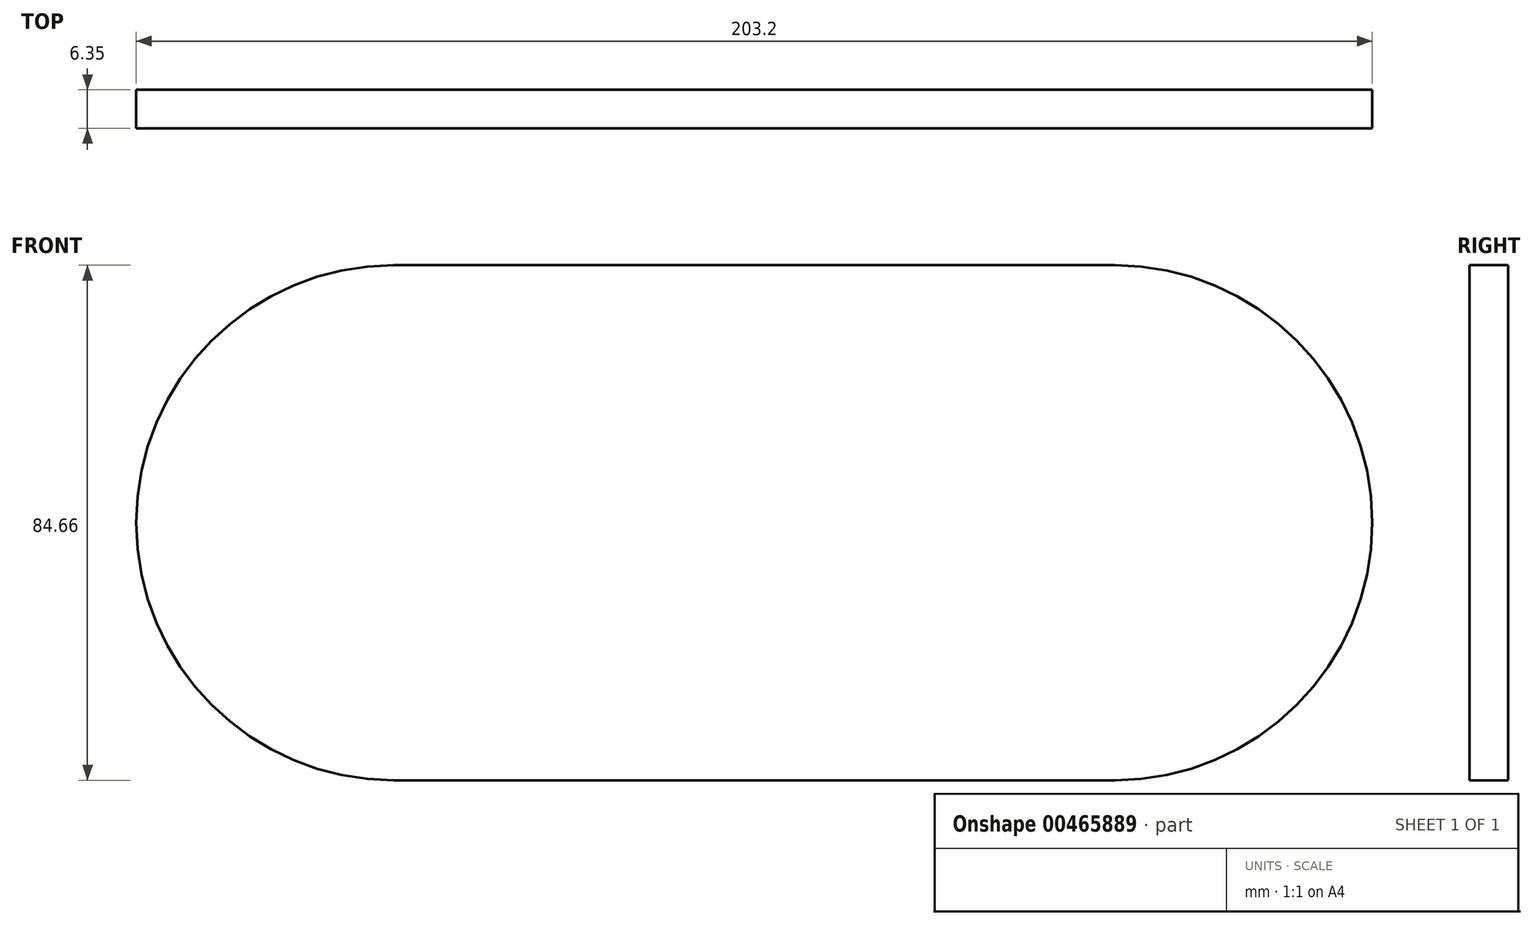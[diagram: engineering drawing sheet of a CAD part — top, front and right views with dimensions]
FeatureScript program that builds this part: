
annotation { "Feature Type Name" : "Feature", "Feature Type Description" : "" }
export const myFeature = defineFeature(function(context is Context, id is Id, definition is map)
    precondition{}
    {
        {
            var Q0;
            Q0=qCreatedBy(makeId("Front.planeOp"),FACE);
            var sketch = newSketch(context, id + "F0", { "sketchPlane" : qUnion([Q0])});
            skLineSegment(sketch, "E0.bottom", {"start": v(-101.6, 42.33) * mm, "end": v(101.6, 42.33) * mm});
            skLineSegment(sketch, "E0.top", {"start": v(-101.6, -42.33) * mm, "end": v(101.6, -42.33) * mm});
            skLineSegment(sketch, "E0.left", {"start": v(-101.6, 42.33) * mm, "end": v(-101.6, -42.33) * mm});
            skLineSegment(sketch, "E0.right", {"start": v(101.6, 42.33) * mm, "end": v(101.6, -42.33) * mm});
            skPoint(sketch, "E0.middle", {"position": v(0, 0) * mm});
            skSolve(sketch);
        }
        {
            var Q0;
            Q0=makeQuery(id+"F0.imprint","IMPRINT",FACE,{"disambiguationData":[TD([[makeQuery(id+"F0.imprint","IMPRINT",EDGE,{"derivedFrom":sQuery(id+"F0.wireOp",EDGE,"E0.bottom")}),-1.0]])]});
            extrude(context, id + "F1", {"entities" : qUnion([Q0]), "depth" : 6.35 * mm, "offsetDistance" : 25.4 * mm});
        }
        {
            var Q0;
            Q0=makeQuery(id+"F1.opExtrude","SWEPT_EDGE",EDGE,{"disambiguationData":[OSD([sQuery(id+"F0.wireOp",EDGE,"E0.bottom"),sQuery(id+"F0.wireOp",EDGE,"E0.left")])]});
            fillet(context, id + "F2", {"entities" : qUnion([Q0]), "radius" : 42.32 * mm, "tangentPropagation" : true, "allowEdgeOverflow" : false});
        }
        {
            var Q0;
            Q0=makeQuery(id+"F1.opExtrude","SWEPT_EDGE",EDGE,{"disambiguationData":[OSD([sQuery(id+"F0.wireOp",EDGE,"E0.top"),sQuery(id+"F0.wireOp",EDGE,"E0.left")])]});
            fillet(context, id + "F3", {"entities" : qUnion([Q0]), "radius" : 42.32 * mm, "tangentPropagation" : true, "allowEdgeOverflow" : false});
        }
        {
            var Q0;
            Q0=makeQuery(id+"F1.opExtrude","SWEPT_EDGE",EDGE,{"disambiguationData":[OSD([sQuery(id+"F0.wireOp",EDGE,"E0.bottom"),sQuery(id+"F0.wireOp",EDGE,"E0.right")])]});
            fillet(context, id + "F4", {"entities" : qUnion([Q0]), "radius" : 42.32 * mm, "tangentPropagation" : true, "allowEdgeOverflow" : false});
        }
        {
            var Q0;
            Q0=makeQuery(id+"F1.opExtrude","SWEPT_EDGE",EDGE,{"disambiguationData":[OSD([sQuery(id+"F0.wireOp",EDGE,"E0.top"),sQuery(id+"F0.wireOp",EDGE,"E0.right")])]});
            fillet(context, id + "F5", {"entities" : qUnion([Q0]), "radius" : 42.32 * mm, "tangentPropagation" : true, "allowEdgeOverflow" : false});
        }
    });
